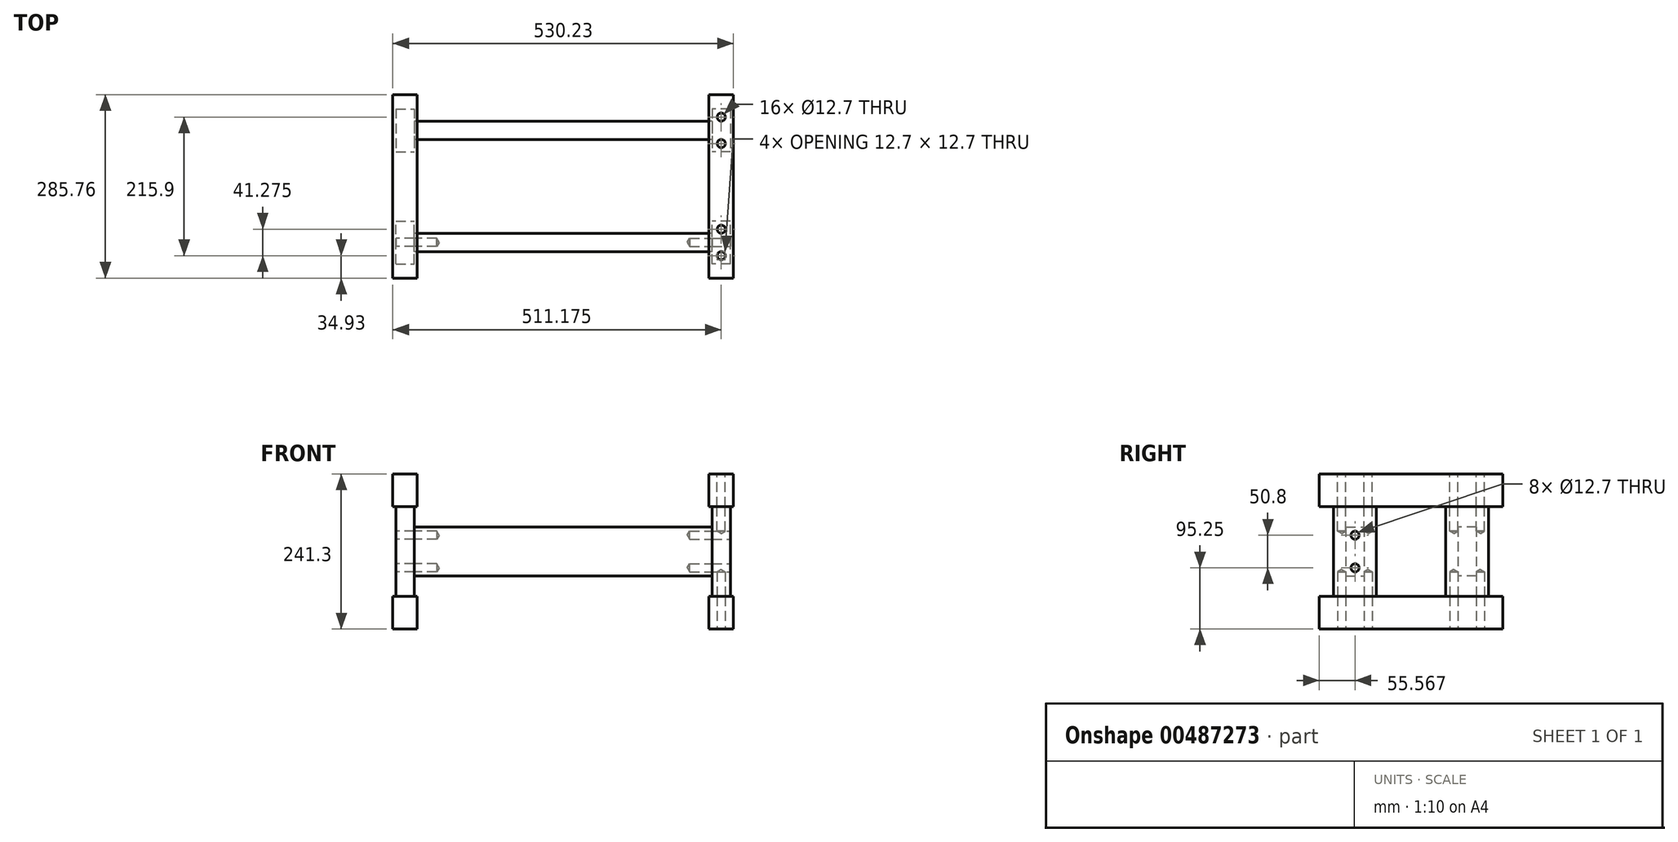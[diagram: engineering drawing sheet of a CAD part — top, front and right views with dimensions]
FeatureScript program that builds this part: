
annotation { "Feature Type Name" : "Feature", "Feature Type Description" : "" }
export const myFeature = defineFeature(function(context is Context, id is Id, definition is map)
    precondition{}
    {
        {
            var Q0;
            Q0=qCreatedBy(makeId("Front.planeOp"),FACE);
            var sketch = newSketch(context, id + "F0", { "sketchPlane" : qUnion([Q0])});
            skLineSegment(sketch, "E0.bottom", {"start": v(-19.05, 25.4) * mm, "end": v(19.05, 25.4) * mm});
            skLineSegment(sketch, "E0.top", {"start": v(-19.05, -25.4) * mm, "end": v(19.05, -25.4) * mm});
            skLineSegment(sketch, "E0.left", {"start": v(-19.05, 25.4) * mm, "end": v(-19.05, -25.4) * mm});
            skLineSegment(sketch, "E0.right", {"start": v(19.05, 25.4) * mm, "end": v(19.05, -25.4) * mm});
            skLineSegment(sketch, "E1", {"start": v(-19.05, 25.4) * mm, "end": v(19.05, -25.4) * mm, "construction": true});
            skSolve(sketch);
        }
        {
            var Q0;
            Q0 = qSketchRegion(id + "F0", true);
            extrude(context, id + "F1", {"entities" : qUnion([Q0]), "depth" : 285.75 * mm, "symmetric" : true});
        }
        {
            var Q0;
            Q0=makeQuery(id+"F1.opExtrude","SWEPT_FACE",FACE,{"disambiguationData":[OSD([sQuery(id+"F0.wireOp",EDGE,"E0.bottom")])]});
            var sketch = newSketch(context, id + "F2", { "sketchPlane" : qUnion([Q0])});
            skLineSegment(sketch, "E2.bottom", {"start": v(-14.29, -120.65) * mm, "end": v(14.29, -120.65) * mm});
            skLineSegment(sketch, "E2.top", {"start": v(-14.29, -53.98) * mm, "end": v(14.29, -53.97) * mm});
            skLineSegment(sketch, "E2.left", {"start": v(-14.29, -120.65) * mm, "end": v(-14.29, -53.98) * mm});
            skLineSegment(sketch, "E2.right", {"start": v(14.29, -120.65) * mm, "end": v(14.29, -53.98) * mm});
            skLineSegment(sketch, "E3", {"start": v(0, 0) * mm, "end": v(-97.9, 0) * mm, "construction": true});
            skLineSegment(sketch, "E4", {"start": v(0, 0) * mm, "end": v(0, -53.98) * mm, "construction": true});
            skSolve(sketch);
        }
        {
            var Q0;
            Q0 = qSketchRegion(id + "F2", true);
            extrude(context, id + "F3", {"entities" : qUnion([Q0]), "depth" : 139.7 * mm});
        }
        {
            var Q0;
            Q0=makeQuery(id+"F3.opExtrude","SWEPT_BODY",BODY,{"disambiguationData":[OSD([sQuery(id+"F2.wireOp",EDGE,"E2.bottom"),sQuery(id+"F2.wireOp",EDGE,"E2.top"),sQuery(id+"F2.wireOp",EDGE,"E2.left"),sQuery(id+"F2.wireOp",EDGE,"E2.right")])]});
            var Q1;
            Q1=qCreatedBy(makeId("Front.planeOp"),FACE);
            mirror(context, id + "F4", {"entities" : qUnion([Q0]), "mirrorPlane" : qUnion([Q1])});
        }
        {
            var Q0;
            Q0=makeQuery(id+"F4.opPattern","COPY",EDGE,{"derivedFrom":makeQuery(id+"F3.opExtrude","SWEPT_EDGE",EDGE,{"disambiguationData":[OSD([sQuery(id+"F2.wireOp",EDGE,"E2.top"),sQuery(id+"F2.wireOp",EDGE,"E2.right")])]}),"instanceName":"1"});
            cPoint(context, id + "F5", {"entities" : qUnion([Q0]), "parameter" : 0.5});
        }
        {
            var Q0;
            Q0 = qCreatedBy(id + "F5" ,VERTEX);
            var Q1;
            Q1=makeQuery(id+"F1.opExtrude","SWEPT_FACE",FACE,{"disambiguationData":[OSD([sQuery(id+"F0.wireOp",EDGE,"E0.bottom")])]});
            cPlane(context, id + "F6", {"entities" : qUnion([Q0, Q1]), "cplaneType" : CPlaneType.PLANE_POINT, "offset" : 25.4 * mm, "width" : 152.4 * mm, "height" : 152.4 * mm});
        }
        {
            var Q0;
            Q0=makeQuery(id+"F1.opExtrude","SWEPT_BODY",BODY,{"disambiguationData":[OSD([sQuery(id+"F0.wireOp",EDGE,"E0.bottom"),sQuery(id+"F0.wireOp",EDGE,"E0.top"),sQuery(id+"F0.wireOp",EDGE,"E0.left"),sQuery(id+"F0.wireOp",EDGE,"E0.right")])]});
            var Q1;
            Q1=qCreatedBy(id+"F6.planeOp",FACE);
            mirror(context, id + "F7", {"entities" : qUnion([Q0]), "mirrorPlane" : qUnion([Q1])});
        }
        {
            var Q0;
            Q0=makeQuery(id+"F3.opExtrude","CAP_EDGE",EDGE,{"disambiguationData":[OSD([sQuery(id+"F2.wireOp",EDGE,"E2.right")])],"isStart":true});
            cPoint(context, id + "F8", {"entities" : qUnion([Q0]), "parameter" : 0.5});
        }
        {
            var Q0;
            Q0 = qCreatedBy(id + "F8" ,VERTEX);
            var Q1;
            Q1=qCreatedBy(makeId("Front.planeOp"),FACE);
            cPlane(context, id + "F9", {"entities" : qUnion([Q0, Q1]), "cplaneType" : CPlaneType.PLANE_POINT, "offset" : 25.4 * mm, "width" : 152.4 * mm, "height" : 152.4 * mm});
        }
        {
            var Q0;
            Q0=makeQuery(id+"F3.opExtrude","SWEPT_FACE",FACE,{"disambiguationData":[OSD([sQuery(id+"F2.wireOp",EDGE,"E2.right")])]});
            var sketch = newSketch(context, id + "F10", { "sketchPlane" : qUnion([Q0])});
            skLineSegment(sketch, "E5.bottom", {"start": v(-101.6, 133.35) * mm, "end": v(-73.02, 133.35) * mm});
            skLineSegment(sketch, "E5.top", {"start": v(-101.6, 57.15) * mm, "end": v(-73.02, 57.15) * mm});
            skLineSegment(sketch, "E5.left", {"start": v(-101.6, 133.35) * mm, "end": v(-101.6, 57.15) * mm});
            skLineSegment(sketch, "E5.right", {"start": v(-73.03, 133.35) * mm, "end": v(-73.03, 57.15) * mm});
            skPoint(sketch, "E6", {"position": v(-87.31, 133.35) * mm});
            skPoint(sketch, "E7", {"position": v(-73.02, 95.25) * mm});
            skSolve(sketch);
        }
        {
            var Q0;
            Q0 = qSketchRegion(id + "F10", true);
            extrude(context, id + "F11", {"entities" : qUnion([Q0]), "depth" : 463.55 * mm});
        }
        {
            var Q0;
            Q0=makeQuery(id+"F11.opExtrude","SWEPT_BODY",BODY,{"disambiguationData":[OSD([sQuery(id+"F10.wireOp",EDGE,"E5.bottom"),sQuery(id+"F10.wireOp",EDGE,"E5.top"),sQuery(id+"F10.wireOp",EDGE,"E5.left"),sQuery(id+"F10.wireOp",EDGE,"E5.right")])]});
            var Q1;
            Q1=qCreatedBy(makeId("Front.planeOp"),FACE);
            mirror(context, id + "F12", {"entities" : qUnion([Q0]), "mirrorPlane" : qUnion([Q1])});
        }
        {
            var Q0;
            Q0=makeQuery(id+"F11.opExtrude","SWEPT_EDGE",EDGE,{"disambiguationData":[OSD([sQuery(id+"F10.wireOp",EDGE,"E5.bottom"),sQuery(id+"F10.wireOp",EDGE,"E5.left")])]});
            cPoint(context, id + "F13", {"entities" : qUnion([Q0]), "parameter" : 0.5});
        }
        {
            var Q0;
            Q0 = qCreatedBy(id + "F13" ,VERTEX);
            var Q1;
            Q1=makeQuery(id+"F11.opExtrude","CAP_FACE",FACE,{"disambiguationData":[OSD([sQuery(id+"F10.wireOp",EDGE,"E5.bottom"),sQuery(id+"F10.wireOp",EDGE,"E5.top"),sQuery(id+"F10.wireOp",EDGE,"E5.left"),sQuery(id+"F10.wireOp",EDGE,"E5.right")])],"isStart":false});
            cPlane(context, id + "F14", {"entities" : qUnion([Q0, Q1]), "cplaneType" : CPlaneType.PLANE_POINT, "offset" : 25.4 * mm, "width" : 152.4 * mm, "height" : 152.4 * mm});
        }
        {
            var Q0;
            Q0=makeQuery(id+"F1.opExtrude","SWEPT_BODY",BODY,{"disambiguationData":[OSD([sQuery(id+"F0.wireOp",EDGE,"E0.bottom"),sQuery(id+"F0.wireOp",EDGE,"E0.top"),sQuery(id+"F0.wireOp",EDGE,"E0.left"),sQuery(id+"F0.wireOp",EDGE,"E0.right")])]});
            var Q1;
            Q1=makeQuery(id+"F3.opExtrude","SWEPT_BODY",BODY,{"disambiguationData":[OSD([sQuery(id+"F2.wireOp",EDGE,"E2.bottom"),sQuery(id+"F2.wireOp",EDGE,"E2.top"),sQuery(id+"F2.wireOp",EDGE,"E2.left"),sQuery(id+"F2.wireOp",EDGE,"E2.right")])]});
            var Q2;
            Q2=makeQuery(id+"F4.opPattern","COPY",BODY,{"derivedFrom":makeQuery(id+"F3.opExtrude","SWEPT_BODY",BODY,{"disambiguationData":[OSD([sQuery(id+"F2.wireOp",EDGE,"E2.bottom"),sQuery(id+"F2.wireOp",EDGE,"E2.top"),sQuery(id+"F2.wireOp",EDGE,"E2.left"),sQuery(id+"F2.wireOp",EDGE,"E2.right")])]}),"instanceName":"1"});
            var Q3;
            Q3=makeQuery(id+"F7.opPattern","COPY",BODY,{"derivedFrom":makeQuery(id+"F1.opExtrude","SWEPT_BODY",BODY,{"disambiguationData":[OSD([sQuery(id+"F0.wireOp",EDGE,"E0.bottom"),sQuery(id+"F0.wireOp",EDGE,"E0.top"),sQuery(id+"F0.wireOp",EDGE,"E0.left"),sQuery(id+"F0.wireOp",EDGE,"E0.right")])]}),"instanceName":"1"});
            var Q4;
            Q4=qCreatedBy(id+"F14.planeOp",FACE);
            mirror(context, id + "F15", {"entities" : qUnion([Q0, Q1, Q2, Q3]), "mirrorPlane" : qUnion([Q4])});
        }
        {
            var Q0;
            Q0=makeQuery(id+"F15.opPattern","COPY",FACE,{"derivedFrom":makeQuery(id+"F7.opPattern","COPY",FACE,{"derivedFrom":makeQuery(id+"F1.opExtrude","SWEPT_FACE",FACE,{"disambiguationData":[OSD([sQuery(id+"F0.wireOp",EDGE,"E0.top")])]}),"instanceName":"1"}),"instanceName":"1"});
            var sketch = newSketch(context, id + "F16", { "sketchPlane" : qUnion([Q0])});
            skLineSegment(sketch, "E8", {"start": v(492.13, 120.65) * mm, "end": v(492.13, 53.97) * mm, "construction": true});
            skLineSegment(sketch, "E9", {"start": v(492.13, -53.98) * mm, "end": v(492.13, -120.65) * mm, "construction": true});
            skPoint(sketch, "E10", {"position": v(492.13, 107.95) * mm});
            skPoint(sketch, "E11", {"position": v(492.13, 66.67) * mm});
            skPoint(sketch, "E12", {"position": v(492.13, -66.68) * mm});
            skPoint(sketch, "E13", {"position": v(492.13, -107.95) * mm});
            skSolve(sketch);
        }
        {
            var Q0;
            Q0=sQuery(id+"F16.wireOp",VERTEX,"E10");
            var Q1;
            Q1=sQuery(id+"F16.wireOp",VERTEX,"E11");
            var Q2;
            Q2=sQuery(id+"F16.wireOp",VERTEX,"E12");
            var Q3;
            Q3=sQuery(id+"F16.wireOp",VERTEX,"E13");
            var Q4;
            Q4=makeQuery(id+"F15.opPattern","COPY",BODY,{"derivedFrom":makeQuery(id+"F1.opExtrude","SWEPT_BODY",BODY,{"disambiguationData":[OSD([sQuery(id+"F0.wireOp",EDGE,"E0.bottom"),sQuery(id+"F0.wireOp",EDGE,"E0.top"),sQuery(id+"F0.wireOp",EDGE,"E0.left"),sQuery(id+"F0.wireOp",EDGE,"E0.right")])]}),"instanceName":"1"});
            var Q5;
            Q5=makeQuery(id+"F15.opPattern","COPY",BODY,{"derivedFrom":makeQuery(id+"F4.opPattern","COPY",BODY,{"derivedFrom":makeQuery(id+"F3.opExtrude","SWEPT_BODY",BODY,{"disambiguationData":[OSD([sQuery(id+"F2.wireOp",EDGE,"E2.bottom"),sQuery(id+"F2.wireOp",EDGE,"E2.top"),sQuery(id+"F2.wireOp",EDGE,"E2.left"),sQuery(id+"F2.wireOp",EDGE,"E2.right")])]}),"instanceName":"1"}),"instanceName":"1"});
            var Q6;
            Q6=makeQuery(id+"F15.opPattern","COPY",BODY,{"derivedFrom":makeQuery(id+"F7.opPattern","COPY",BODY,{"derivedFrom":makeQuery(id+"F1.opExtrude","SWEPT_BODY",BODY,{"disambiguationData":[OSD([sQuery(id+"F0.wireOp",EDGE,"E0.bottom"),sQuery(id+"F0.wireOp",EDGE,"E0.top"),sQuery(id+"F0.wireOp",EDGE,"E0.left"),sQuery(id+"F0.wireOp",EDGE,"E0.right")])]}),"instanceName":"1"}),"instanceName":"1"});
            var Q7;
            Q7=makeQuery(id+"F15.opPattern","COPY",BODY,{"derivedFrom":makeQuery(id+"F3.opExtrude","SWEPT_BODY",BODY,{"disambiguationData":[OSD([sQuery(id+"F2.wireOp",EDGE,"E2.bottom"),sQuery(id+"F2.wireOp",EDGE,"E2.top"),sQuery(id+"F2.wireOp",EDGE,"E2.left"),sQuery(id+"F2.wireOp",EDGE,"E2.right")])]}),"instanceName":"1"});
            hole(context, id + "F17", {"style" : HoleStyle.SIMPLE, "endStyle" : HoleEndStyle.BLIND, "holeDiameter" : 12.7 * mm, "holeDepth" : 88.9 * mm, "isTappedThrough" : true, "tappedDepth" : 12.7 * mm, "tapClearance" : 3, "locations" : qUnion([Q0, Q1, Q2, Q3]), "scope" : qUnion([Q4, Q5, Q6, Q7])});
        }
        {
            var Q0;
            Q0=makeQuery(id+"F15.opPattern","COPY",FACE,{"derivedFrom":makeQuery(id+"F3.opExtrude","SWEPT_FACE",FACE,{"disambiguationData":[OSD([sQuery(id+"F2.wireOp",EDGE,"E2.left")])]}),"instanceName":"1"});
            var sketch = newSketch(context, id + "F18", { "sketchPlane" : qUnion([Q0])});
            skLineSegment(sketch, "E14", {"start": v(-87.31, 165.1) * mm, "end": v(-87.31, 25.4) * mm, "construction": true});
            skPoint(sketch, "E15", {"position": v(-87.31, 120.65) * mm});
            skPoint(sketch, "E16", {"position": v(-87.31, 69.85) * mm});
            skSolve(sketch);
        }
        {
            var Q0;
            Q0=sQuery(id+"F18.wireOp",VERTEX,"E15");
            var Q1;
            Q1=sQuery(id+"F18.wireOp",VERTEX,"E16");
            var Q2;
            Q2=makeQuery(id+"F11.opExtrude","SWEPT_BODY",BODY,{"disambiguationData":[OSD([sQuery(id+"F10.wireOp",EDGE,"E5.bottom"),sQuery(id+"F10.wireOp",EDGE,"E5.top"),sQuery(id+"F10.wireOp",EDGE,"E5.left"),sQuery(id+"F10.wireOp",EDGE,"E5.right")])]});
            var Q3;
            Q3=makeQuery(id+"F15.opPattern","COPY",BODY,{"derivedFrom":makeQuery(id+"F3.opExtrude","SWEPT_BODY",BODY,{"disambiguationData":[OSD([sQuery(id+"F2.wireOp",EDGE,"E2.bottom"),sQuery(id+"F2.wireOp",EDGE,"E2.top"),sQuery(id+"F2.wireOp",EDGE,"E2.left"),sQuery(id+"F2.wireOp",EDGE,"E2.right")])]}),"instanceName":"1"});
            hole(context, id + "F19", {"style" : HoleStyle.SIMPLE, "endStyle" : HoleEndStyle.BLIND, "holeDiameter" : 12.7 * mm, "holeDepth" : 63.5 * mm, "isTappedThrough" : true, "tappedDepth" : 12.7 * mm, "tapClearance" : 3, "locations" : qUnion([Q0, Q1]), "scope" : qUnion([Q2, Q3])});
        }
        {
            var Q0;
            Q0=makeQuery(id+"F15.opPattern","COPY",FACE,{"derivedFrom":makeQuery(id+"F1.opExtrude","SWEPT_FACE",FACE,{"disambiguationData":[OSD([sQuery(id+"F0.wireOp",EDGE,"E0.top")])]}),"instanceName":"1"});
            var sketch = newSketch(context, id + "F20", { "sketchPlane" : qUnion([Q0])});
            skPoint(sketch, "E17", {"position": v(492.13, 107.95) * mm});
            skPoint(sketch, "E18", {"position": v(492.13, 66.68) * mm});
            skPoint(sketch, "E19", {"position": v(492.13, -66.67) * mm});
            skPoint(sketch, "E20", {"position": v(492.13, -107.95) * mm});
            skSolve(sketch);
        }
        {
            var Q0;
            Q0=sQuery(id+"F20.wireOp",VERTEX,"E20");
            var Q1;
            Q1=sQuery(id+"F20.wireOp",VERTEX,"E19");
            var Q2;
            Q2=sQuery(id+"F20.wireOp",VERTEX,"E18");
            var Q3;
            Q3=sQuery(id+"F20.wireOp",VERTEX,"E17");
            var Q4;
            Q4=makeQuery(id+"F15.opPattern","COPY",BODY,{"derivedFrom":makeQuery(id+"F1.opExtrude","SWEPT_BODY",BODY,{"disambiguationData":[OSD([sQuery(id+"F0.wireOp",EDGE,"E0.bottom"),sQuery(id+"F0.wireOp",EDGE,"E0.top"),sQuery(id+"F0.wireOp",EDGE,"E0.left"),sQuery(id+"F0.wireOp",EDGE,"E0.right")])]}),"instanceName":"1"});
            var Q5;
            Q5=makeQuery(id+"F15.opPattern","COPY",BODY,{"derivedFrom":makeQuery(id+"F3.opExtrude","SWEPT_BODY",BODY,{"disambiguationData":[OSD([sQuery(id+"F2.wireOp",EDGE,"E2.bottom"),sQuery(id+"F2.wireOp",EDGE,"E2.top"),sQuery(id+"F2.wireOp",EDGE,"E2.left"),sQuery(id+"F2.wireOp",EDGE,"E2.right")])]}),"instanceName":"1"});
            var Q6;
            Q6=makeQuery(id+"F15.opPattern","COPY",BODY,{"derivedFrom":makeQuery(id+"F4.opPattern","COPY",BODY,{"derivedFrom":makeQuery(id+"F3.opExtrude","SWEPT_BODY",BODY,{"disambiguationData":[OSD([sQuery(id+"F2.wireOp",EDGE,"E2.bottom"),sQuery(id+"F2.wireOp",EDGE,"E2.top"),sQuery(id+"F2.wireOp",EDGE,"E2.left"),sQuery(id+"F2.wireOp",EDGE,"E2.right")])]}),"instanceName":"1"}),"instanceName":"1"});
            hole(context, id + "F21", {"style" : HoleStyle.SIMPLE, "endStyle" : HoleEndStyle.BLIND, "holeDiameter" : 12.7 * mm, "holeDepth" : 88.9 * mm, "isTappedThrough" : true, "tappedDepth" : 12.7 * mm, "tapClearance" : 3, "locations" : qUnion([Q0, Q1, Q2, Q3]), "scope" : qUnion([Q4, Q5, Q6])});
        }
        {
            var Q0;
            Q0=makeQuery(id+"F3.opExtrude","SWEPT_FACE",FACE,{"disambiguationData":[OSD([sQuery(id+"F2.wireOp",EDGE,"E2.left")])]});
            var sketch = newSketch(context, id + "F22", { "sketchPlane" : qUnion([Q0])});
            skPoint(sketch, "E21", {"position": v(87.31, 69.85) * mm});
            skPoint(sketch, "E22", {"position": v(87.31, 120.65) * mm});
            skSolve(sketch);
        }
        {
            var Q0;
            Q0=sQuery(id+"F22.wireOp",VERTEX,"E21");
            var Q1;
            Q1=sQuery(id+"F22.wireOp",VERTEX,"E22");
            var Q2;
            Q2=makeQuery(id+"F3.opExtrude","SWEPT_BODY",BODY,{"disambiguationData":[OSD([sQuery(id+"F2.wireOp",EDGE,"E2.bottom"),sQuery(id+"F2.wireOp",EDGE,"E2.top"),sQuery(id+"F2.wireOp",EDGE,"E2.left"),sQuery(id+"F2.wireOp",EDGE,"E2.right")])]});
            var Q3;
            Q3=makeQuery(id+"F11.opExtrude","SWEPT_BODY",BODY,{"disambiguationData":[OSD([sQuery(id+"F10.wireOp",EDGE,"E5.bottom"),sQuery(id+"F10.wireOp",EDGE,"E5.top"),sQuery(id+"F10.wireOp",EDGE,"E5.left"),sQuery(id+"F10.wireOp",EDGE,"E5.right")])]});
            hole(context, id + "F23", {"style" : HoleStyle.SIMPLE, "endStyle" : HoleEndStyle.BLIND, "holeDiameter" : 12.7 * mm, "holeDepth" : 63.5 * mm, "isTappedThrough" : true, "tappedDepth" : 12.7 * mm, "tapClearance" : 3, "locations" : qUnion([Q0, Q1]), "scope" : qUnion([Q2, Q3])});
        }
    });
